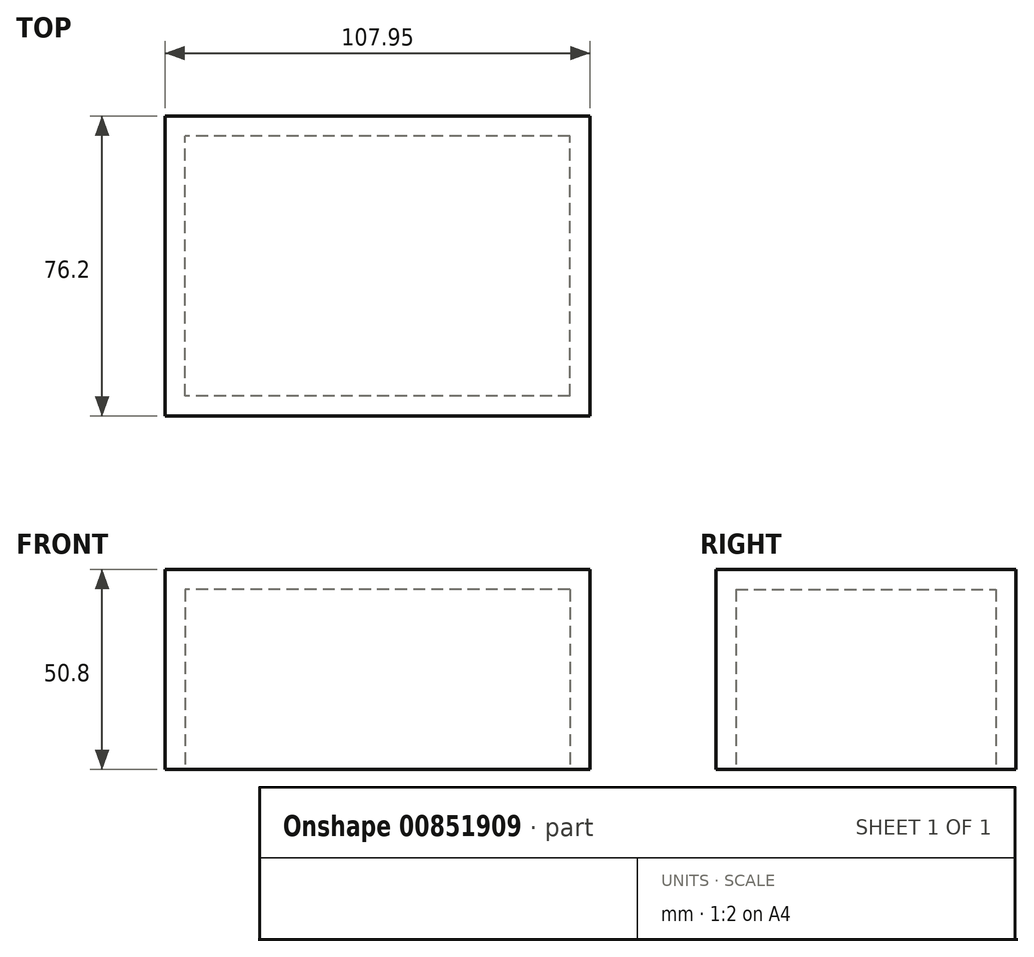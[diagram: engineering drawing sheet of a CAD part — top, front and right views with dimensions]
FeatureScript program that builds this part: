
annotation { "Feature Type Name" : "Feature", "Feature Type Description" : "" }
export const myFeature = defineFeature(function(context is Context, id is Id, definition is map)
    precondition{}
    {
        {
            var Q0;
            Q0=qCreatedBy(makeId("Top.planeOp"),FACE);
            var sketch = newSketch(context, id + "F0", { "sketchPlane" : qUnion([Q0])});
            skLineSegment(sketch, "E0.bottom", {"start": v(0, 0) * mm, "end": v(107.95, 0) * mm});
            skLineSegment(sketch, "E0.top", {"start": v(0, 76.2) * mm, "end": v(107.95, 76.2) * mm});
            skLineSegment(sketch, "E0.left", {"start": v(0, 0) * mm, "end": v(0, 76.2) * mm});
            skLineSegment(sketch, "E0.right", {"start": v(107.95, 0) * mm, "end": v(107.95, 76.2) * mm});
            skLineSegment(sketch, "E1.bottom", {"start": v(102.87, 71.12) * mm, "end": v(5.08, 71.12) * mm});
            skLineSegment(sketch, "E1.top", {"start": v(102.87, 5.08) * mm, "end": v(5.08, 5.08) * mm});
            skLineSegment(sketch, "E1.left", {"start": v(102.87, 71.12) * mm, "end": v(102.87, 5.08) * mm});
            skLineSegment(sketch, "E1.right", {"start": v(5.08, 71.12) * mm, "end": v(5.08, 5.08) * mm});
            skPoint(sketch, "E1.middle", {"position": v(53.97, 38.1) * mm});
            skPoint(sketch, "E1.middle.positionSnap0", {"position": v(53.97, 0) * mm});
            skPoint(sketch, "E1.middle.positionSnap1", {"position": v(0, 38.1) * mm});
            skPoint(sketch, "E1.centerSnap0", {"position": v(53.97, 0) * mm});
            skPoint(sketch, "E1.centerSnap1", {"position": v(0, 38.1) * mm});
            skSolve(sketch);
        }
        {
            var Q0;
            Q0=makeQuery(id+"F0.imprint","IMPRINT",FACE,{"disambiguationData":[TD([[makeQuery(id+"F0.imprint","IMPRINT",EDGE,{"derivedFrom":sQuery(id+"F0.wireOp",EDGE,"E0.bottom")}),1.0]])]});
            var Q1;
            Q1=makeQuery(id+"F0.imprint","IMPRINT",FACE,{"disambiguationData":[TD([[makeQuery(id+"F0.imprint","IMPRINT",EDGE,{"derivedFrom":sQuery(id+"F0.wireOp",EDGE,"E1.bottom")}),1.0]])]});
            extrude(context, id + "F1", {"entities" : qUnion([Q0, Q1]), "depth" : 50.8 * mm, "offsetDistance" : 25.4 * mm});
        }
        {
            var Q0;
            Q0=makeQuery(id+"F1.opExtrude","CAP_FACE",FACE,{"disambiguationData":[OSD([sQuery(id+"F0.wireOp",EDGE,"E0.bottom"),sQuery(id+"F0.wireOp",EDGE,"E0.top"),sQuery(id+"F0.wireOp",EDGE,"E0.left"),sQuery(id+"F0.wireOp",EDGE,"E0.right")])],"isStart":true});
            var sketch = newSketch(context, id + "F2", { "sketchPlane" : qUnion([Q0])});
            skLineSegment(sketch, "E2.bottom", {"start": v(102.87, -5.08) * mm, "end": v(5.08, -5.08) * mm});
            skLineSegment(sketch, "E2.top", {"start": v(102.87, -71.12) * mm, "end": v(5.08, -71.12) * mm});
            skLineSegment(sketch, "E2.left", {"start": v(102.87, -5.08) * mm, "end": v(102.87, -71.12) * mm});
            skLineSegment(sketch, "E2.right", {"start": v(5.08, -5.08) * mm, "end": v(5.08, -71.12) * mm});
            skPoint(sketch, "E2.middle", {"position": v(53.97, -38.1) * mm});
            skPoint(sketch, "E2.middle.positionSnap0", {"position": v(53.97, -76.2) * mm});
            skPoint(sketch, "E2.middle.positionSnap1", {"position": v(0, -38.1) * mm});
            skPoint(sketch, "E2.centerSnap0", {"position": v(53.97, -76.2) * mm});
            skPoint(sketch, "E2.centerSnap1", {"position": v(0, -38.1) * mm});
            skSolve(sketch);
        }
        {
            var Q0;
            Q0=makeQuery(id+"F2.imprint","IMPRINT",FACE,{"disambiguationData":[TD([[makeQuery(id+"F2.imprint","IMPRINT",EDGE,{"derivedFrom":sQuery(id+"F2.wireOp",EDGE,"E2.bottom")}),1.0]])]});
            extrude(context, id + "F3", {"entities" : qUnion([Q0]), "operationType" : NewBodyOperationType.REMOVE, "oppositeDirection" : true, "depth" : 45.72 * mm, "offsetDistance" : 25.4 * mm});
        }
    });
